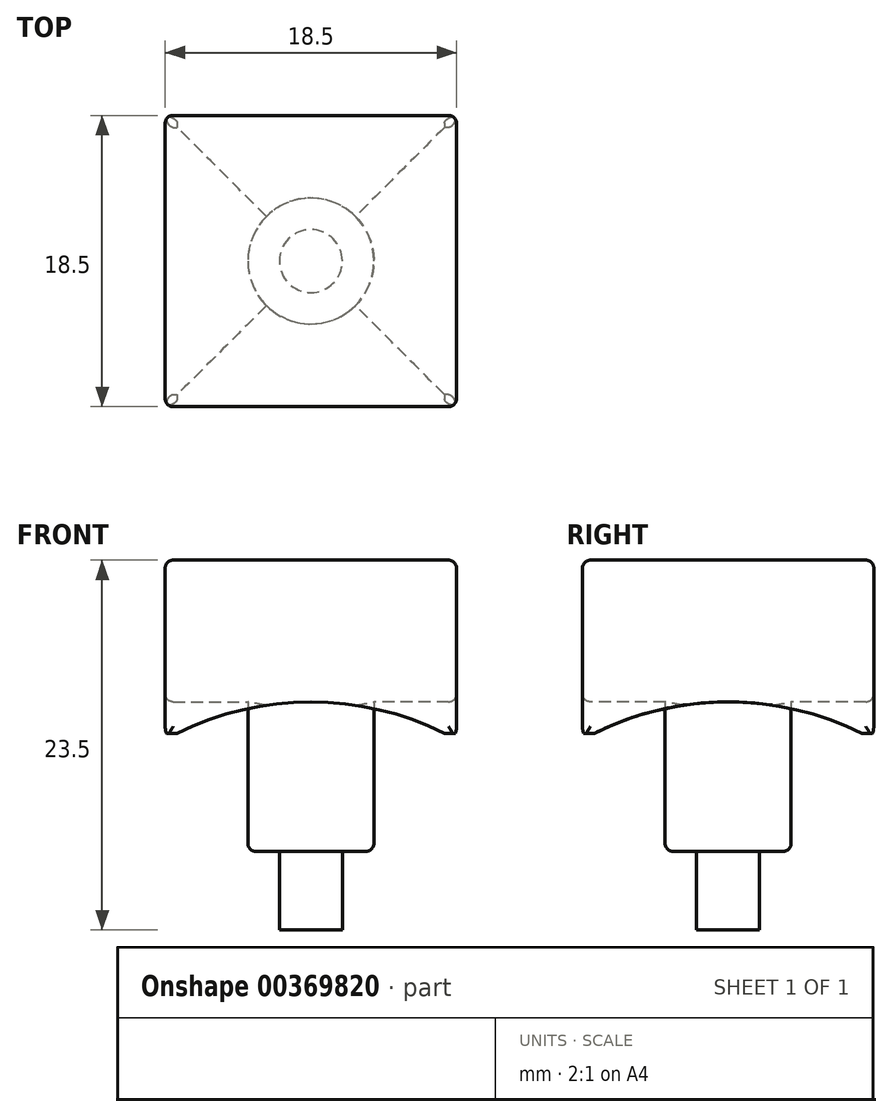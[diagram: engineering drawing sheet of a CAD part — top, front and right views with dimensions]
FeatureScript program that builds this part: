
annotation { "Feature Type Name" : "Feature", "Feature Type Description" : "" }
export const myFeature = defineFeature(function(context is Context, id is Id, definition is map)
    precondition{}
    {
        {
            var Q0;
            Q0=qCreatedBy(makeId("Front.planeOp"),FACE);
            var sketch = newSketch(context, id + "F0", { "sketchPlane" : qUnion([Q0])});
            skLineSegment(sketch, "E0.rect.bottom", {"start": v(9.25, 5.5) * mm, "end": v(-9.25, 5.5) * mm});
            skLineSegment(sketch, "E0.rect.top", {"start": v(9.25, -5.5) * mm, "end": v(-9.25, -5.5) * mm});
            skLineSegment(sketch, "E0.rect.left", {"start": v(9.25, 5.5) * mm, "end": v(9.25, -5.5) * mm});
            skLineSegment(sketch, "E0.rect.right", {"start": v(-9.25, 5.5) * mm, "end": v(-9.25, -5.5) * mm});
            skPoint(sketch, "E0.rect.middle", {"position": v(0, 0) * mm});
            skSolve(sketch);
        }
        {
            var Q0;
            Q0=makeQuery(id+"F0.imprint","IMPRINT",FACE,{"disambiguationData":[TD([[makeQuery(id+"F0.imprint","IMPRINT",EDGE,{"derivedFrom":sQuery(id+"F0.wireOp",EDGE,"E0.rect.bottom")}),1.0]])]});
            extrude(context, id + "F1", {"entities" : qUnion([Q0]), "oppositeDirection" : true, "depth" : 9.25 * mm});
        }
        {
            var Q0;
            Q0=qSketchRegion(id+"F0",true);
            extrude(context, id + "F2", {"entities" : qUnion([Q0]), "operationType" : NewBodyOperationType.ADD, "depth" : 9.25 * mm});
        }
        {
            var Q0;
            Q0=qCreatedBy(makeId("Front.planeOp"),FACE);
            var sketch = newSketch(context, id + "F3", { "sketchPlane" : qUnion([Q0])});
            skPoint(sketch, "E1", {"position": v(0, -3.5) * mm});
            skCircle(sketch, "E2", {"center": v(0, -22.5) * mm, "radius": 19 * mm});
            skSolve(sketch);
        }
        {
            var Q0;
            Q0=qCreatedBy(makeId("Right.planeOp"),FACE);
            var sketch = newSketch(context, id + "F4", { "sketchPlane" : qUnion([Q0])});
            skPoint(sketch, "E3", {"position": v(0, -3.5) * mm});
            skCircle(sketch, "E4", {"center": v(0, -22.5) * mm, "radius": 19 * mm});
            skSolve(sketch);
        }
        {
            var Q0;
            Q0=qSketchRegion(id+"F9",true);
            var Q1;
            Q1=qSketchRegion(id+"F3",true);
            extrude(context, id + "F5", {"entities" : qUnion([Q0, Q1]), "operationType" : NewBodyOperationType.REMOVE, "oppositeDirection" : true, "depth" : 25.4 * mm});
        }
        {
            var Q0;
            Q0=qSketchRegion(id+"F3",true);
            extrude(context, id + "F6", {"entities" : qUnion([Q0]), "operationType" : NewBodyOperationType.REMOVE, "depth" : 25.4 * mm});
        }
        {
            var Q0;
            Q0=qSketchRegion(id+"F4",true);
            extrude(context, id + "F7", {"entities" : qUnion([Q0]), "operationType" : NewBodyOperationType.REMOVE, "oppositeDirection" : true, "depth" : 25.4 * mm});
        }
        {
            var Q0;
            Q0=qSketchRegion(id+"F4",true);
            extrude(context, id + "F8", {"entities" : qUnion([Q0]), "operationType" : NewBodyOperationType.REMOVE, "depth" : 25.4 * mm});
        }
        {
            var Q0;
            {var subQ0=sQuery(id+"F0.wireOp",EDGE,"E0.rect.top");Q0=makeQuery(id+"F2.boolean.opBoolean","MERGE",FACE,{"derivedFrom":[makeQuery(id+"F1.opExtrude","SWEPT_FACE",FACE,{"disambiguationData":[OSD([subQ0])]}),makeQuery(id+"F2.opExtrude","SWEPT_FACE",FACE,{"disambiguationData":[OSD([subQ0])]})]});}
            var sketch = newSketch(context, id + "F9", { "sketchPlane" : qUnion([Q0])});
            skCircle(sketch, "E5", {"center": v(0, 0) * mm, "radius": 4 * mm});
            skSolve(sketch);
        }
        {
            var Q0;
            Q0=qSketchRegion(id+"F9",true);
            extrude(context, id + "F10", {"entities" : qUnion([Q0]), "operationType" : NewBodyOperationType.ADD, "oppositeDirection" : true, "depth" : 3.46 * mm});
        }
        {
            var Q0;
            Q0=makeQuery(id+"F10.opExtrude","CAP_FACE",FACE,{"disambiguationData":[OSD([sQuery(id+"F9.wireOp",EDGE,"E5")])],"isStart":true});
            extrude(context, id + "F11", {"entities" : qUnion([Q0]), "operationType" : NewBodyOperationType.ADD, "depth" : 7.5 * mm});
        }
        {
            var Q0;
            Q0=makeQuery(id+"F2.opExtrude","CAP_EDGE",EDGE,{"disambiguationData":[OSD([sQuery(id+"F0.wireOp",EDGE,"E0.rect.left")])],"isStart":false});
            var Q1;
            Q1=makeQuery(id+"F2.opExtrude","CAP_EDGE",EDGE,{"disambiguationData":[OSD([sQuery(id+"F0.wireOp",EDGE,"E0.rect.bottom")])],"isStart":false});
            var Q2;
            {var subQ0=sQuery(id+"F0.wireOp",EDGE,"E0.rect.bottom");var subQ1=sQuery(id+"F0.wireOp",EDGE,"E0.rect.left");Q2=makeQuery(id+"F2.boolean.opBoolean","MERGE",EDGE,{"derivedFrom":[makeQuery(id+"F1.opExtrude","SWEPT_EDGE",EDGE,{"disambiguationData":[OSD([subQ0,subQ1])]}),makeQuery(id+"F2.opExtrude","SWEPT_EDGE",EDGE,{"disambiguationData":[OSD([subQ0,subQ1])]})]});}
            var Q3;
            Q3=makeQuery(id+"F1.opExtrude","CAP_EDGE",EDGE,{"disambiguationData":[OSD([sQuery(id+"F0.wireOp",EDGE,"E0.rect.bottom")])],"isStart":false});
            var Q4;
            {var subQ0=sQuery(id+"F0.wireOp",EDGE,"E0.rect.bottom");var subQ1=sQuery(id+"F0.wireOp",EDGE,"E0.rect.right");Q4=makeQuery(id+"F2.boolean.opBoolean","MERGE",EDGE,{"derivedFrom":[makeQuery(id+"F1.opExtrude","SWEPT_EDGE",EDGE,{"disambiguationData":[OSD([subQ0,subQ1])]}),makeQuery(id+"F2.opExtrude","SWEPT_EDGE",EDGE,{"disambiguationData":[OSD([subQ0,subQ1])]})]});}
            var Q5;
            Q5=makeQuery(id+"F2.opExtrude","CAP_EDGE",EDGE,{"disambiguationData":[OSD([sQuery(id+"F0.wireOp",EDGE,"E0.rect.right")])],"isStart":false});
            var Q6;
            Q6=makeQuery(id+"F1.opExtrude","CAP_EDGE",EDGE,{"disambiguationData":[OSD([sQuery(id+"F0.wireOp",EDGE,"E0.rect.left")])],"isStart":false});
            var Q7;
            Q7=makeQuery(id+"F1.opExtrude","CAP_EDGE",EDGE,{"disambiguationData":[OSD([sQuery(id+"F0.wireOp",EDGE,"E0.rect.right")])],"isStart":false});
            var Q8;
            Q8=makeQuery(id+"F11.opExtrude","CAP_EDGE",EDGE,{"disambiguationData":[OSD([sQuery(id+"F9.wireOp",EDGE,"E5")])],"isStart":false});
            var Q9;
            Q9=makeQuery(id+"F6.boolean.opBoolean","INTERSECT",EDGE,{"derivedFrom":[makeQuery(id+"F2.opExtrude","CAP_FACE",FACE,{"disambiguationData":[OSD([sQuery(id+"F0.wireOp",EDGE,"E0.rect.bottom"),sQuery(id+"F0.wireOp",EDGE,"E0.rect.top"),sQuery(id+"F0.wireOp",EDGE,"E0.rect.left"),sQuery(id+"F0.wireOp",EDGE,"E0.rect.right")])],"isStart":false}),makeQuery(id+"F6.opExtrude","SWEPT_FACE",FACE,{"disambiguationData":[OSD([sQuery(id+"F3.wireOp",EDGE,"E2")])]})]});
            var Q10;
            {var subQ0=sQuery(id+"F0.wireOp",EDGE,"E0.rect.right");Q10=makeQuery(id+"F7.boolean.opBoolean","INTERSECT",EDGE,{"derivedFrom":[makeQuery(id+"F2.boolean.opBoolean","MERGE",FACE,{"derivedFrom":[makeQuery(id+"F1.opExtrude","SWEPT_FACE",FACE,{"disambiguationData":[OSD([subQ0])]}),makeQuery(id+"F2.opExtrude","SWEPT_FACE",FACE,{"disambiguationData":[OSD([subQ0])]})]}),makeQuery(id+"F7.opExtrude","SWEPT_FACE",FACE,{"disambiguationData":[OSD([sQuery(id+"F4.wireOp",EDGE,"E4")])]})]});}
            var Q11;
            {var subQ0=sQuery(id+"F0.wireOp",EDGE,"E0.rect.left");Q11=makeQuery(id+"F8.boolean.opBoolean","INTERSECT",EDGE,{"derivedFrom":[makeQuery(id+"F2.boolean.opBoolean","MERGE",FACE,{"derivedFrom":[makeQuery(id+"F1.opExtrude","SWEPT_FACE",FACE,{"disambiguationData":[OSD([subQ0])]}),makeQuery(id+"F2.opExtrude","SWEPT_FACE",FACE,{"disambiguationData":[OSD([subQ0])]})]}),makeQuery(id+"F8.opExtrude","SWEPT_FACE",FACE,{"disambiguationData":[OSD([sQuery(id+"F4.wireOp",EDGE,"E4")])]})]});}
            var Q12;
            Q12=makeQuery(id+"F5.boolean.opBoolean","INTERSECT",EDGE,{"derivedFrom":[makeQuery(id+"F1.opExtrude","CAP_FACE",FACE,{"disambiguationData":[OSD([sQuery(id+"F0.wireOp",EDGE,"E0.rect.bottom"),sQuery(id+"F0.wireOp",EDGE,"E0.rect.top"),sQuery(id+"F0.wireOp",EDGE,"E0.rect.left"),sQuery(id+"F0.wireOp",EDGE,"E0.rect.right")])],"isStart":false}),makeQuery(id+"F5.opExtrude","SWEPT_FACE",FACE,{"disambiguationData":[OSD([sQuery(id+"F3.wireOp",EDGE,"E2")])]})]});
            fillet(context, id + "F12", {"entities" : qUnion([Q0, Q1, Q2, Q3, Q4, Q5, Q6, Q7, Q8, Q9, Q10, Q11, Q12]), "radius" : .5 * mm, "tangentPropagation" : true, "allowEdgeOverflow" : false});
        }
        {
            var Q0;
            Q0=makeQuery(id+"F11.opExtrude","CAP_FACE",FACE,{"disambiguationData":[OSD([sQuery(id+"F9.wireOp",EDGE,"E5")])],"isStart":false});
            var sketch = newSketch(context, id + "F13", { "sketchPlane" : qUnion([Q0])});
            skCircle(sketch, "E6", {"center": v(0, 0) * mm, "radius": 2 * mm});
            skSolve(sketch);
        }
        {
            var Q0;
            Q0=makeQuery(id+"F13.imprint","IMPRINT",FACE,{"disambiguationData":[TD([[makeQuery(id+"F13.imprint","IMPRINT",EDGE,{"derivedFrom":sQuery(id+"F13.wireOp",EDGE,"E6")}),1.0]])]});
            extrude(context, id + "F14", {"entities" : qUnion([Q0]), "operationType" : NewBodyOperationType.ADD, "depth" : 5 * mm});
        }
    });
